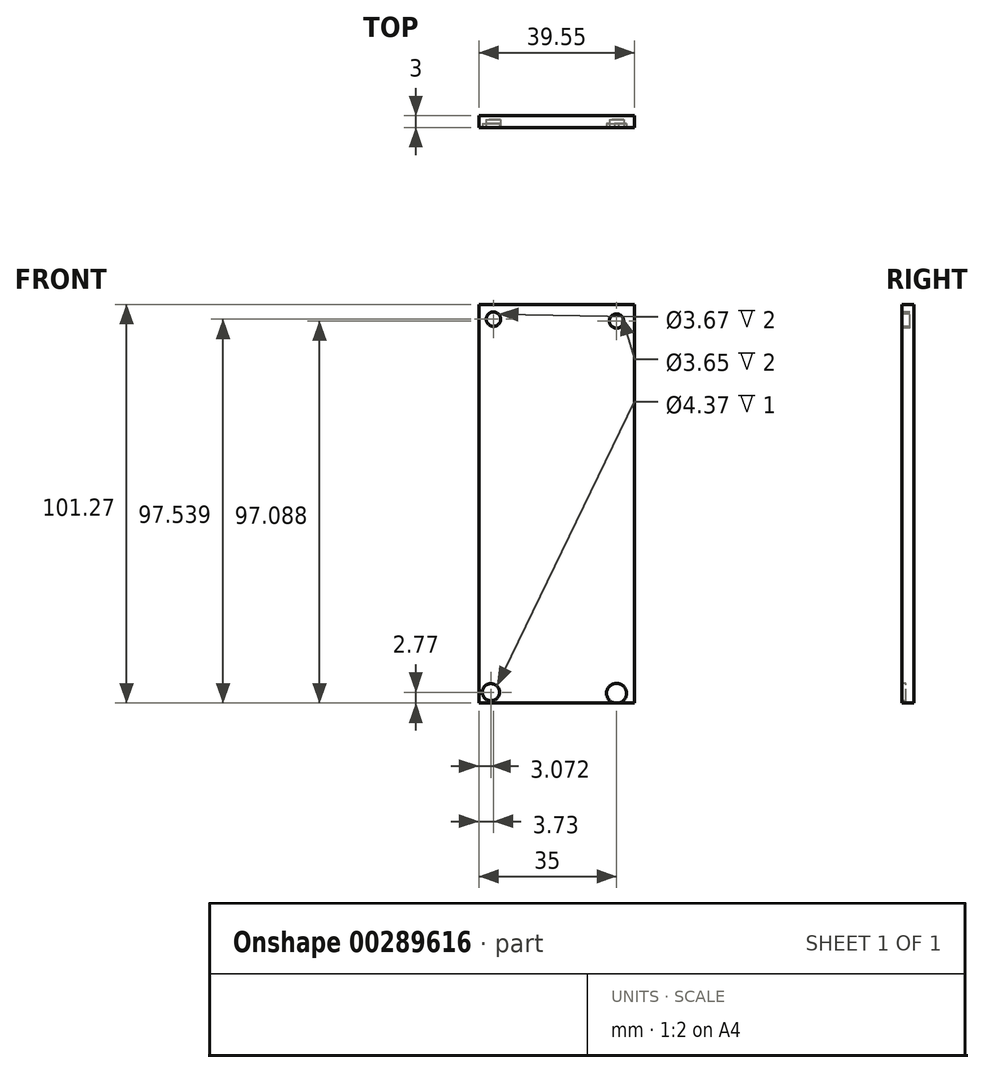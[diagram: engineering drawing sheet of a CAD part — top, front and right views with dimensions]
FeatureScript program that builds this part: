
annotation { "Feature Type Name" : "Feature", "Feature Type Description" : "" }
export const myFeature = defineFeature(function(context is Context, id is Id, definition is map)
    precondition{}
    {
        {
            var Q0;
            Q0=qCreatedBy(makeId("Front.planeOp"),FACE);
            var sketch = newSketch(context, id + "F0", { "sketchPlane" : qUnion([Q0])});
            skLineSegment(sketch, "E0.bottom", {"start": v(-35, 46.62) * mm, "end": v(29.55, 46.62) * mm});
            skLineSegment(sketch, "E0.top", {"start": v(-35, -54.65) * mm, "end": v(29.55, -54.65) * mm});
            skLineSegment(sketch, "E0.left", {"start": v(-35, 46.62) * mm, "end": v(-35, -54.65) * mm});
            skLineSegment(sketch, "E0.right", {"start": v(29.55, 46.62) * mm, "end": v(29.55, -54.65) * mm});
            skSolve(sketch);
        }
        {
            var Q0;
            Q0 = qSketchRegion(id + "F0", true);
            extrude(context, id + "F1", {"entities" : qUnion([Q0]), "depth" : 5 * mm, "hasSecondDirection" : true, "secondDirectionOppositeDirection" : true, "secondDirectionDepth" : 25 * mm, "symmetric" : true});
        }
        {
            var Q0;
            Q0=makeQuery(id+"F1.opExtrude","CAP_FACE",FACE,{"disambiguationData":[OSD([sQuery(id+"F0.wireOp",EDGE,"E0.bottom"),sQuery(id+"F0.wireOp",EDGE,"E0.top"),sQuery(id+"F0.wireOp",EDGE,"E0.left"),sQuery(id+"F0.wireOp",EDGE,"E0.right")])],"isStart":false});
            extrude(context, id + "F2", {"entities" : qUnion([Q0]), "operationType" : NewBodyOperationType.REMOVE, "oppositeDirection" : true, "depth" : 2 * mm});
        }
        {
            var Q0;
            Q0=makeQuery(id+"F2.boolean.opBoolean","COPY",FACE,{"derivedFrom":makeQuery(id+"F2.opExtrude","CAP_FACE",FACE,{"disambiguationData":[OSD([sQuery(id+"F0.wireOp",EDGE,"E0.bottom"),sQuery(id+"F0.wireOp",EDGE,"E0.top"),sQuery(id+"F0.wireOp",EDGE,"E0.left"),sQuery(id+"F0.wireOp",EDGE,"E0.right")])],"isStart":false})});
            var sketch = newSketch(context, id + "F3", { "sketchPlane" : qUnion([Q0])});
            skCircle(sketch, "E1", {"center": v(-31.27, 42.89) * mm, "radius": 1.84 * mm});
            skCircle(sketch, "E2", {"center": v(24.93, 42.55) * mm, "radius": 2.16 * mm});
            skSolve(sketch);
        }
        {
            var Q0;
            Q0=makeQuery(id+"F3.imprint","IMPRINT",FACE,{"disambiguationData":[TD([[makeQuery(id+"F3.imprint","IMPRINT",EDGE,{"derivedFrom":sQuery(id+"F3.wireOp",EDGE,"E1")}),1.0]])]});
            var Q1;
            Q1=makeQuery(id+"F3.imprint","IMPRINT",FACE,{"disambiguationData":[TD([[makeQuery(id+"F3.imprint","IMPRINT",EDGE,{"derivedFrom":sQuery(id+"F3.wireOp",EDGE,"E2")}),1.0]])]});
            extrude(context, id + "F4", {"entities" : qUnion([Q0, Q1]), "operationType" : NewBodyOperationType.REMOVE, "oppositeDirection" : true, "depth" : 2 * mm});
        }
        {
            var Q0;
            Q0=makeQuery(id+"F1.opExtrude","SWEPT_FACE",FACE,{"disambiguationData":[OSD([sQuery(id+"F0.wireOp",EDGE,"E0.right")])]});
            extrude(context, id + "F5", {"entities" : qUnion([Q0]), "operationType" : NewBodyOperationType.REMOVE, "oppositeDirection" : true, "depth" : 25 * mm});
        }
        {
            var Q0;
            Q0=makeQuery(id+"F2.boolean.opBoolean","COPY",FACE,{"derivedFrom":makeQuery(id+"F2.opExtrude","CAP_FACE",FACE,{"disambiguationData":[OSD([sQuery(id+"F0.wireOp",EDGE,"E0.bottom"),sQuery(id+"F0.wireOp",EDGE,"E0.top"),sQuery(id+"F0.wireOp",EDGE,"E0.left"),sQuery(id+"F0.wireOp",EDGE,"E0.right")])],"isStart":false})});
            var sketch = newSketch(context, id + "F6", { "sketchPlane" : qUnion([Q0])});
            skCircle(sketch, "E3", {"center": v(0, 42.44) * mm, "radius": 1.83 * mm});
            skSolve(sketch);
        }
        {
            var Q0;
            Q0=makeQuery(id+"F6.imprint","IMPRINT",FACE,{"disambiguationData":[TD([[makeQuery(id+"F6.imprint","IMPRINT",EDGE,{"derivedFrom":sQuery(id+"F6.wireOp",EDGE,"E3")}),1.0]])]});
            extrude(context, id + "F7", {"entities" : qUnion([Q0]), "operationType" : NewBodyOperationType.REMOVE, "oppositeDirection" : true, "depth" : 2 * mm});
        }
        {
            var Q0;
            Q0=makeQuery(id+"F2.boolean.opBoolean","COPY",FACE,{"derivedFrom":makeQuery(id+"F2.opExtrude","CAP_FACE",FACE,{"disambiguationData":[OSD([sQuery(id+"F0.wireOp",EDGE,"E0.bottom"),sQuery(id+"F0.wireOp",EDGE,"E0.top"),sQuery(id+"F0.wireOp",EDGE,"E0.left"),sQuery(id+"F0.wireOp",EDGE,"E0.right")])],"isStart":false})});
            var sketch = newSketch(context, id + "F8", { "sketchPlane" : qUnion([Q0])});
            skCircle(sketch, "E4", {"center": v(-31.93, -51.88) * mm, "radius": 2.18 * mm});
            skCircle(sketch, "E5", {"center": v(0, -52.16) * mm, "radius": 2.53 * mm});
            skSolve(sketch);
        }
        {
            var Q0;
            Q0=makeQuery(id+"F8.imprint","IMPRINT",FACE,{"disambiguationData":[TD([[makeQuery(id+"F8.imprint","IMPRINT",EDGE,{"derivedFrom":sQuery(id+"F8.wireOp",EDGE,"E4")}),1.0]])]});
            var Q1;
            {var subQ0=sQuery(id+"F8.wireOp",EDGE,"E5");var subQ1=makeQuery(id+"F2.boolean.opBoolean","COPY",EDGE,{"derivedFrom":makeQuery(id+"F2.opExtrude","CAP_EDGE",EDGE,{"disambiguationData":[OSD([sQuery(id+"F0.wireOp",EDGE,"E0.top")])],"isStart":false})});var subQ2=makeQuery(id+"F8.imprint","INTERSECT",VERTEX,{"disambiguationData":[OD(0.0)],"derivedFrom":[subQ1,subQ0]});Q1=makeQuery(id+"F8.imprint","IMPRINT",FACE,{"disambiguationData":[TD([[makeQuery(id+"F8.imprint","IMPRINT",EDGE,{"disambiguationData":[TD([[subQ2,1.0]])],"derivedFrom":subQ0}),1.0]])]});}
            extrude(context, id + "F9", {"entities" : qUnion([Q0, Q1]), "operationType" : NewBodyOperationType.REMOVE, "oppositeDirection" : true, "depth" : 2 * mm, "symmetric" : true});
        }
    });
